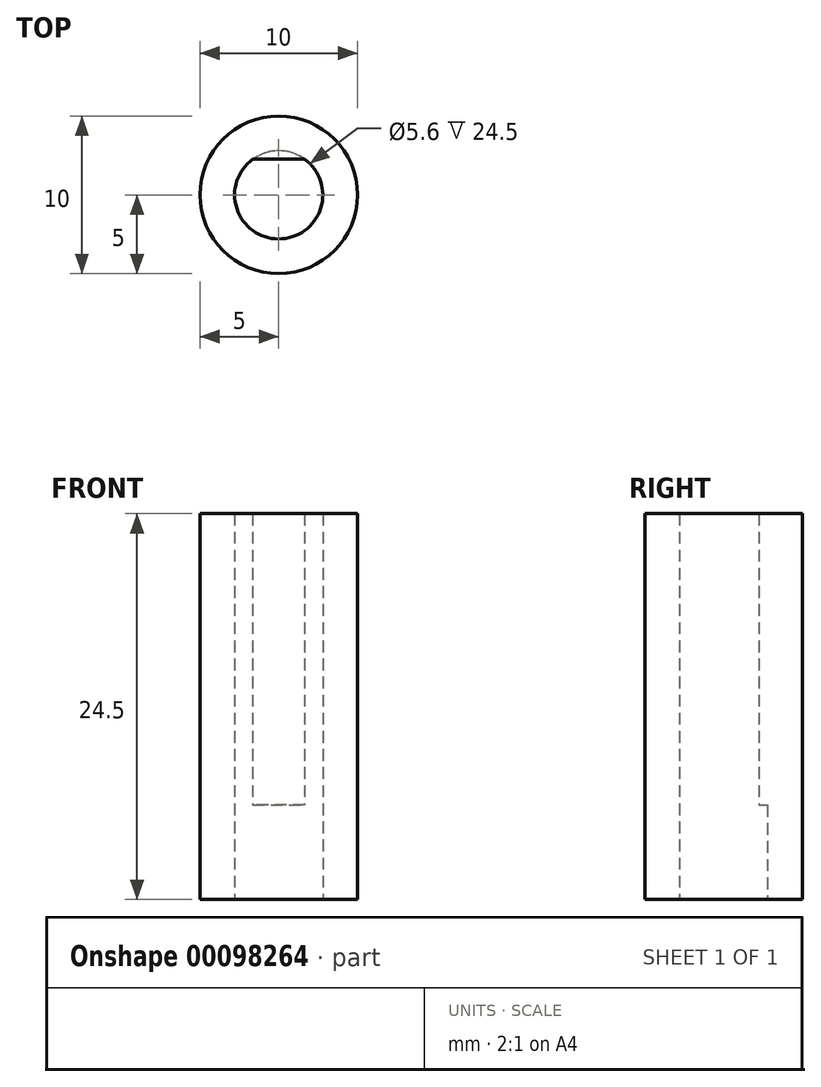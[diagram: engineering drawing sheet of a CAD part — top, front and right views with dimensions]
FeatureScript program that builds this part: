
annotation { "Feature Type Name" : "Feature", "Feature Type Description" : "" }
export const myFeature = defineFeature(function(context is Context, id is Id, definition is map)
    precondition{}
    {
        {
            var Q0;
            Q0=qCreatedBy(makeId("Top.planeOp"),FACE);
            var sketch = newSketch(context, id + "F0", { "sketchPlane" : qUnion([Q0])});
            skCircle(sketch, "E0", {"center": v(0, 0) * mm, "radius": 32.65 * mm});
            skCircle(sketch, "E1", {"center": v(0, 0) * mm, "radius": 37.65 * mm});
            skCircle(sketch, "E2", {"center": v(0, 0) * mm, "radius": 2.8 * mm});
            skLineSegment(sketch, "E3", {"start": v(-1.75, 2.19) * mm, "end": v(1.75, 2.19) * mm});
            skCircle(sketch, "E4", {"center": v(0, 0) * mm, "radius": 5 * mm});
            skSolve(sketch);
        }
        {
            var Q0;
            Q0=makeQuery(id+"F0.imprint","IMPRINT",FACE,{"disambiguationData":[TD([[makeQuery(id+"F0.imprint","IMPRINT",EDGE,{"derivedFrom":sQuery(id+"F0.wireOp",EDGE,"E4")}),1.0]])]});
            extrude(context, id + "F1", {"entities" : qUnion([Q0]), "depth" : 6 * mm});
        }
        {
            var Q0;
            Q0=makeQuery(id+"F1.opExtrude","CAP_FACE",FACE,{"disambiguationData":[OSD([sQuery(id+"F0.wireOp",EDGE,"E2"),sQuery(id+"F0.wireOp",EDGE,"E4")])],"isStart":false});
            var sketch = newSketch(context, id + "F2", { "sketchPlane" : qUnion([Q0])});
            skLineSegment(sketch, "E5", {"start": v(-1.65, 2.26) * mm, "end": v(1.65, 2.26) * mm});
            skSolve(sketch);
        }
        {
            var Q0;
            Q0 = qSketchRegion(id + "F2", true);
            var Q1;
            Q1=makeQuery(id+"F2.imprint","IMPRINT",FACE,{"disambiguationData":[TD([[makeQuery(id+"F2.imprint","IMPRINT",EDGE,{"derivedFrom":makeQuery(id+"F1.opExtrude","CAP_EDGE",EDGE,{"disambiguationData":[OSD([sQuery(id+"F0.wireOp",EDGE,"E4")])],"isStart":false})}),1.0]])]});
            var Q2;
            {var subQ0=sQuery(id+"F2.wireOp",EDGE,"E5");Q2=makeQuery(id+"F2.imprint","IMPRINT",FACE,{"disambiguationData":[TD([[makeQuery(id+"F2.imprint","IMPRINT",EDGE,{"derivedFrom":subQ0}),1.0]])]});}
            extrude(context, id + "F3", {"entities" : qUnion([Q0, Q1, Q2]), "operationType" : NewBodyOperationType.ADD, "depth" : 18.5 * mm});
        }
    });
